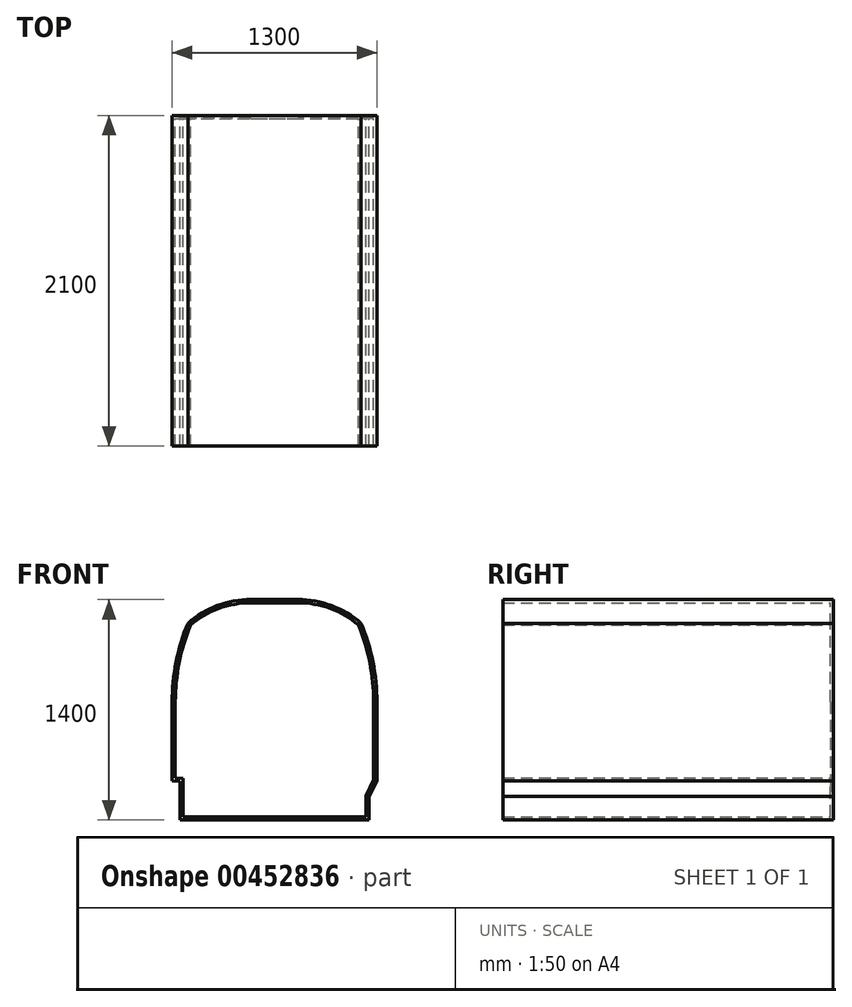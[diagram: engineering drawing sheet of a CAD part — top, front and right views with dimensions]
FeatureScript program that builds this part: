
annotation { "Feature Type Name" : "Feature", "Feature Type Description" : "" }
export const myFeature = defineFeature(function(context is Context, id is Id, definition is map)
    precondition{}
    {
        {
            var Q0;
            Q0=qCreatedBy(makeId("Front.planeOp"),FACE);
            var sketch = newSketch(context, id + "F0", { "sketchPlane" : qUnion([Q0])});
            skLineSegment(sketch, "E0", {"start": v(-600, 0) * mm, "end": v(600, 0) * mm});
            skLineSegment(sketch, "E1", {"start": v(-600, 0) * mm, "end": v(-600, 300) * mm});
            skLineSegment(sketch, "E2", {"start": v(600, 0) * mm, "end": v(600, 300) * mm});
            skLineSegment(sketch, "E3", {"start": v(-600, 300) * mm, "end": v(600, 300) * mm, "construction": true});
            skLineSegment(sketch, "E4", {"start": v(-150, 1400) * mm, "end": v(150, 1400) * mm});
            skLineSegment(sketch, "E5", {"start": v(0, 0) * mm, "end": v(0, 1400) * mm, "construction": true});
            skLineSegment(sketch, "E6", {"start": v(-550, 1250) * mm, "end": v(550, 1250) * mm, "construction": true});
            skPoint(sketch, "E7", {"position": v(0, 1250) * mm});
            skArc(sketch, "E8", {"start": v(-150, 1400) * mm, "mid": v(-363.6, 1361.27) * mm, "end": v(-550, 1250) * mm});
            skArc(sketch, "E9", {"start": v(150, 1400) * mm, "mid": v(363.6, 1361.27) * mm, "end": v(550, 1250) * mm});
            skArc(sketch, "E10", {"start": v(-650, 750) * mm, "mid": v(-624.75, 1004.95) * mm, "end": v(-550, 1250) * mm});
            skPoint(sketch, "E11", {"position": v(-586.93, 1150) * mm});
            skCircle(sketch, "E12", {"center": v(-586.93, 1150) * mm, "radius": 902.2 * mm, "construction": true});
            skLineSegment(sketch, "E13", {"start": v(-1150, 300) * mm, "end": v(-350, 300) * mm, "construction": true});
            skLineSegment(sketch, "E14", {"start": v(-1150, 300) * mm, "end": v(-1150, 445.07) * mm, "construction": true});
            skLineSegment(sketch, "E15", {"start": v(-650, 750) * mm, "end": v(-650, 250) * mm});
            skArc(sketch, "E16.MirrorCS", {"start": v(650, 750) * mm, "mid": v(624.75, 1004.95) * mm, "end": v(550, 1250) * mm});
            skLineSegment(sketch, "E17.MirrorCS", {"start": v(650, 750) * mm, "end": v(650, 250) * mm});
            skLineSegment(sketch, "E18", {"start": v(650, 250) * mm, "end": v(600, 150) * mm});
            skLineSegment(sketch, "E19", {"start": v(-650, 250) * mm, "end": v(-600, 246.5) * mm});
            skSolve(sketch);
        }
        {
            var Q0;
            {var subQ0=sQuery(id+"F0.wireOp",EDGE,"E0");Q0=makeQuery(id+"F0.imprint","IMPRINT",FACE,{"disambiguationData":[TD([[makeQuery(id+"F0.imprint","IMPRINT",EDGE,{"derivedFrom":subQ0}),1.0]])]});}
            extrude(context, id + "F1", {"entities" : qUnion([Q0]), "depth" : 2100 * mm});
        }
        {
            var Q0;
            Q0=makeQuery(id+"F1.opExtrude","CAP_FACE",FACE,{"disambiguationData":[OSD([sQuery(id+"F0.wireOp",EDGE,"E0"),sQuery(id+"F0.wireOp",EDGE,"E1"),sQuery(id+"F0.wireOp",EDGE,"E2"),sQuery(id+"F0.wireOp",EDGE,"E4"),sQuery(id+"F0.wireOp",EDGE,"E8"),sQuery(id+"F0.wireOp",EDGE,"E9"),sQuery(id+"F0.wireOp",EDGE,"E10"),sQuery(id+"F0.wireOp",EDGE,"E15"),sQuery(id+"F0.wireOp",EDGE,"E16.MirrorCS"),sQuery(id+"F0.wireOp",EDGE,"E17.MirrorCS"),sQuery(id+"F0.wireOp",EDGE,"E18"),sQuery(id+"F0.wireOp",EDGE,"E19")])],"isStart":false});
            shell(context, id + "F2", {"entities" : qUnion([Q0]), "thickness" : 20 * mm});
        }
    });
